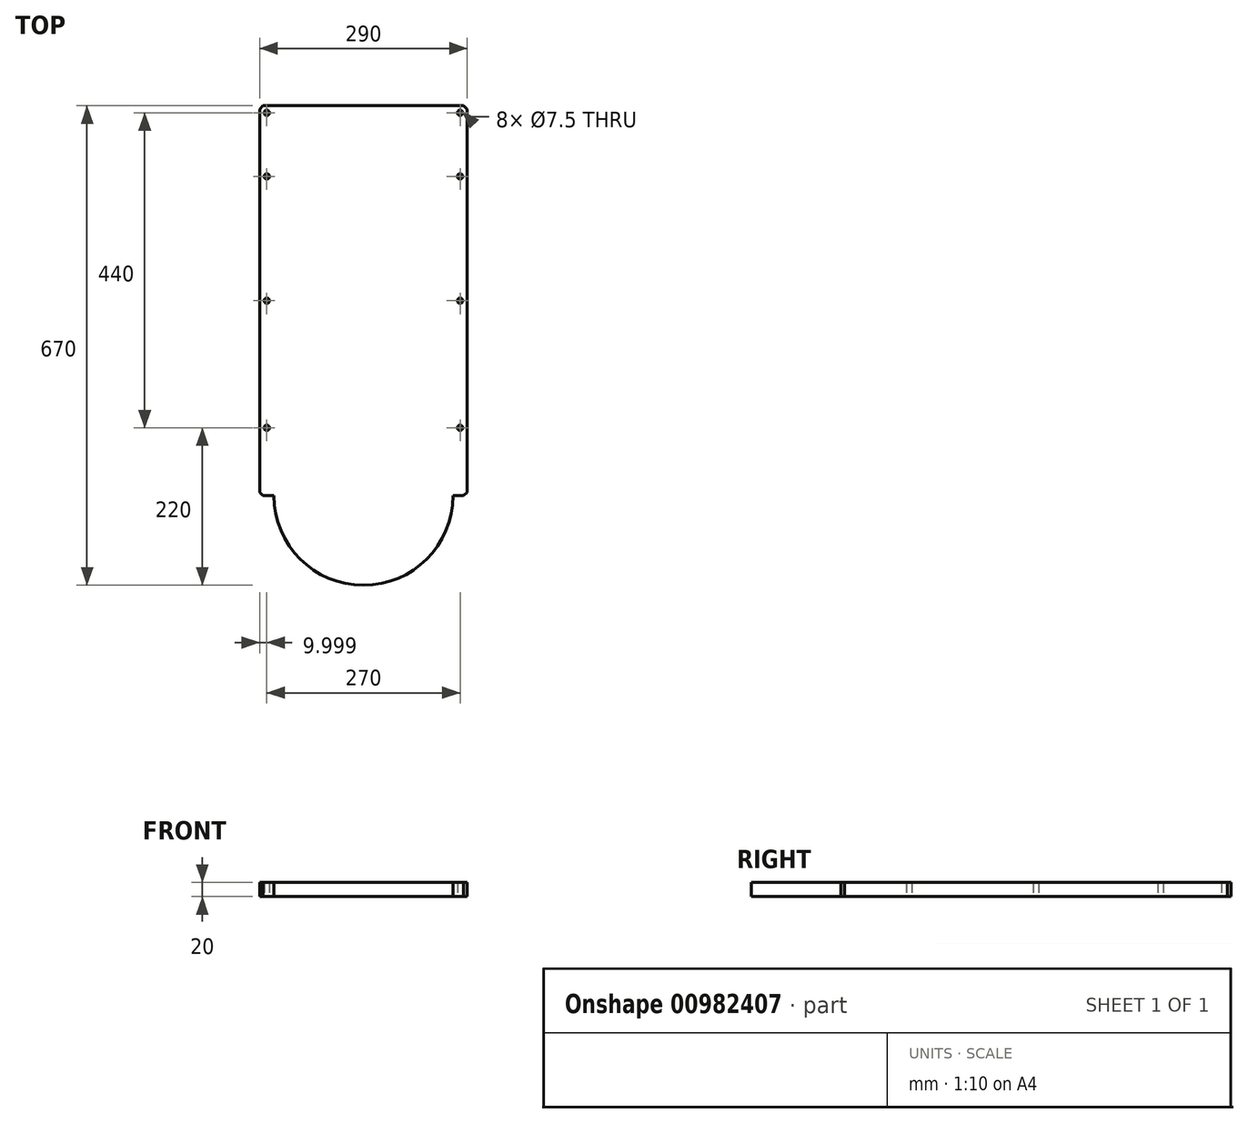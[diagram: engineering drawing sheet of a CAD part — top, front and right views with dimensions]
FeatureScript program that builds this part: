
annotation { "Feature Type Name" : "Feature", "Feature Type Description" : "" }
export const myFeature = defineFeature(function(context is Context, id is Id, definition is map)
    precondition{}
    {
        {
            var Q0;
            Q0=qCreatedBy(makeId("Top.planeOp"),FACE);
            var sketch = newSketch(context, id + "F0", { "sketchPlane" : qUnion([Q0])});
            skLineSegment(sketch, "E0.bottom", {"start": v(95.23, -224.44) * mm, "end": v(75.23, -224.44) * mm});
            skLineSegment(sketch, "E0.top", {"start": v(95.23, 320.56) * mm, "end": v(-194.77, 320.56) * mm});
            skLineSegment(sketch, "E0.left", {"start": v(95.23, -224.44) * mm, "end": v(95.23, 320.56) * mm});
            skLineSegment(sketch, "E0.right", {"start": v(-194.77, -224.44) * mm, "end": v(-194.77, 320.56) * mm});
            skPoint(sketch, "E0.middle", {"position": v(-49.77, 48.06) * mm});
            skPoint(sketch, "E1", {"position": v(-49.77, -224.44) * mm});
            skArc(sketch, "E2", {"start": v(-174.77, -224.44) * mm, "mid": v(-49.77, -349.44) * mm, "end": v(75.23, -224.44) * mm});
            skPoint(sketch, "E3", {"position": v(-174.77, 320.56) * mm});
            skPoint(sketch, "E4", {"position": v(75.23, 320.56) * mm});
            skLineSegment(sketch, "E5", {"start": v(-174.77, 320.56) * mm, "end": v(-174.77, 300.56) * mm});
            skLineSegment(sketch, "E6", {"start": v(-174.77, 300.56) * mm, "end": v(-194.77, 300.56) * mm});
            skLineSegment(sketch, "E7", {"start": v(-194.77, 320.56) * mm, "end": v(-174.77, 300.56) * mm});
            skLineSegment(sketch, "E8", {"start": v(-194.77, 300.56) * mm, "end": v(-174.77, 320.56) * mm});
            skPoint(sketch, "E9", {"position": v(-184.77, 310.56) * mm});
            skCircle(sketch, "E10", {"center": v(-184.77, 310.56) * mm, "radius": 3.75 * mm});
            skCircle(sketch, "E11", {"center": v(-184.77, -129.44) * mm, "radius": 3.75 * mm});
            skCircle(sketch, "E12", {"center": v(85.23, 310.56) * mm, "radius": 3.75 * mm});
            skCircle(sketch, "E13", {"center": v(85.23, 221.81) * mm, "radius": 3.75 * mm});
            skCircle(sketch, "E14", {"center": v(85.23, 48.06) * mm, "radius": 3.75 * mm});
            skCircle(sketch, "E15", {"center": v(-184.77, 48.06) * mm, "radius": 3.75 * mm});
            skCircle(sketch, "E16", {"center": v(-184.77, 221.81) * mm, "radius": 3.75 * mm});
            skLineSegment(sketch, "E17.trimOffspring", {"start": v(-174.77, -224.44) * mm, "end": v(-194.77, -224.44) * mm});
            skCircle(sketch, "E18", {"center": v(85.23, -129.44) * mm, "radius": 3.75 * mm});
            skLineSegment(sketch, "E19", {"start": v(-49.77, -349.44) * mm, "end": v(193.66, -349.44) * mm});
            skSolve(sketch);
        }
        {
            var Q0;
            Q0 = qSketchRegion(id + "F0", true);
            extrude(context, id + "F1", {"entities" : qUnion([Q0]), "depth" : 20 * mm, "offsetDistance" : 25 * mm});
        }
        {
            var Q0;
            Q0=makeQuery(id+"F1.opExtrude","SWEPT_EDGE",EDGE,{"disambiguationData":[OSD([sQuery(id+"F0.wireOp",EDGE,"E0.bottom"),sQuery(id+"F0.wireOp",EDGE,"E0.left")])]});
            var Q1;
            Q1=makeQuery(id+"F1.opExtrude","SWEPT_EDGE",EDGE,{"disambiguationData":[OSD([sQuery(id+"F0.wireOp",EDGE,"E0.right"),sQuery(id+"F0.wireOp",EDGE,"E17.trimOffspring")])]});
            var Q2;
            Q2=makeQuery(id+"F1.opExtrude","SWEPT_EDGE",EDGE,{"disambiguationData":[OSD([sQuery(id+"F0.wireOp",EDGE,"E0.top"),sQuery(id+"F0.wireOp",EDGE,"E0.left")])]});
            var Q3;
            Q3=makeQuery(id+"F1.opExtrude","SWEPT_EDGE",EDGE,{"disambiguationData":[OSD([sQuery(id+"F0.wireOp",EDGE,"E0.top"),sQuery(id+"F0.wireOp",EDGE,"E0.right"),sQuery(id+"F0.wireOp",EDGE,"E7")])]});
            chamfer(context, id + "F2", {"entities" : qUnion([Q0, Q1, Q2, Q3]), "width" : 5 * mm, "tangentPropagation" : true});
        }
    });
